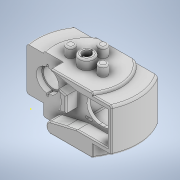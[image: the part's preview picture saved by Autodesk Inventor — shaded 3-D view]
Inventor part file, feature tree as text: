
AUTODESK INVENTOR PART (.ipt)
format: ipt  version: 2021 (Build 250183000, 183)  size: 771,072 bytes
history: native  units: mm
features: sketch x23, extrude x18, fillet x5, other x1, loft x1
ambient origin geometry x8: Origin, YZ Plane, XZ Plane, XY Plane, X Axis, Y Axis, Z Axis, Center Point
bodies: Body1 (feature_tree)
feature tree (48):
  other  "Bryła1"
  extrude  "Wyciągnięcie proste1"  Depth=95.0mm
  extrude  "Wyciągnięcie proste2"  Depth=53.0mm TaperAngle=0.0deg
  extrude  "Wyciągnięcie proste3"  Depth=9.0mm TaperAngle=0.0deg
  fillet  "Zaokrąglenie1"  [1 undecoded]
  extrude  "Wyciągnięcie proste4"  Depth=1.5mm
  extrude  "Wyciągnięcie proste5"  TaperAngle=0.0deg  [1 undecoded]
  extrude  "Wyciągnięcie proste7"  Depth=5.0mm TaperAngle=0.0deg
  extrude  "Wyciągnięcie proste8"  Depth=31.0mm
  extrude  "Wyciągnięcie proste9"  Depth=12.5mm
  extrude  "Wyciągnięcie proste10"  Depth=5.0mm TaperAngle=0.0deg
  extrude  "Wyciągnięcie proste11"  Depth=1.0mm
  sketch  "Szkic16"
  extrude  "Wyciągnięcie proste13"  Depth=0.75mm
  sketch  "Szkic19"
  extrude  "Wyciągnięcie proste18"  Depth=32.0mm TaperAngle=0.0deg
  extrude  "Wyciągnięcie proste19"  Depth=1.0mm
  extrude  "Wyciągnięcie proste20"  Depth=1.0mm
  extrude  "Wyciągnięcie proste21"  Depth=32.0mm TaperAngle=0.0deg
  fillet  "Zaokrąglenie2"  Radius=65.0mm
  extrude  "Wyciągnięcie proste22"  Depth=11.0mm TaperAngle=0.0deg
  fillet  "Zaokrąglenie3"  Radius=2.0mm
  extrude  "Wyciągnięcie proste23"  Depth=10.0mm TaperAngle=0.0deg
  fillet  "Zaokrąglenie4"  Radius=37.0mm
  sketch  "Szkic34"
  extrude  "Wyciągnięcie proste24"  Depth=45.0mm
  loft  "Wyciągnięcie złożone1"
  sketch  "Szkic38"
  sketch  "Szkic39"
  fillet  "Zaokrąglenie5"  Radius=2.0mm
  sketch  "Szkic1"
  sketch  "Szkic2"
  sketch  "Szkic3"
  sketch  "Szkic5"
  sketch  "Szkic6"
  sketch  "Szkic10"
  sketch  "Szkic11"
  sketch  "Szkic13"
  sketch  "Szkic14"
  sketch  "Szkic15"
  sketch  "Szkic24"
  sketch  "Szkic26"
  sketch  "Szkic27"
  sketch  "Szkic28"
  sketch  "Szkic33"
  sketch  "Szkic35"
  sketch  "Szkic36"
  sketch  "Szkic37"
note: 2 required parameter values undecoded (feature->parameter linkage not recoverable at this tier; creation-order binding heuristic only, values carry confidence <= 0.55)
